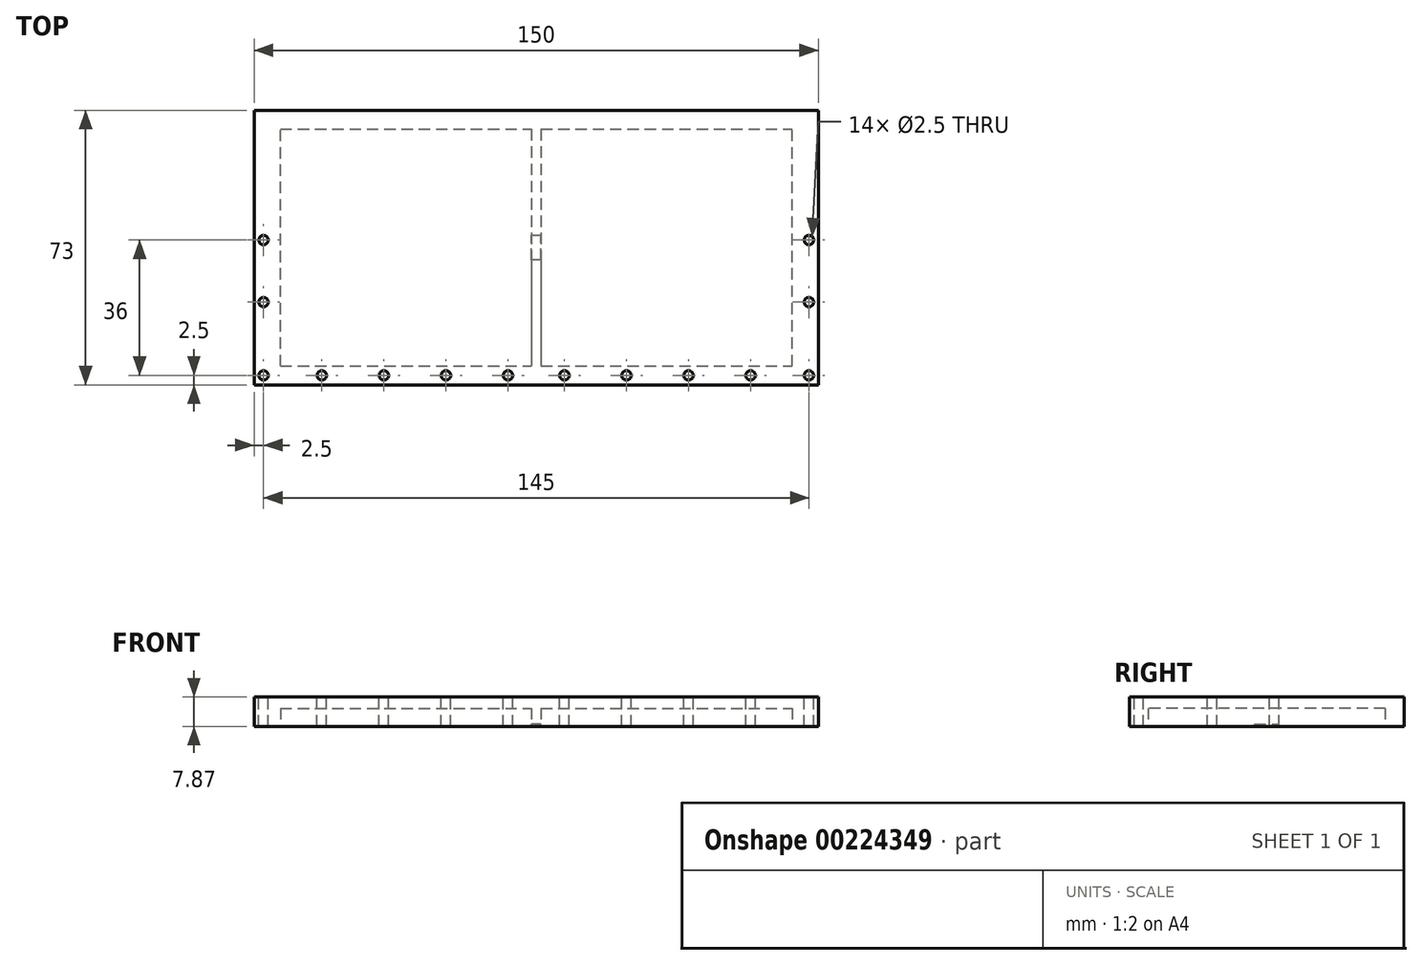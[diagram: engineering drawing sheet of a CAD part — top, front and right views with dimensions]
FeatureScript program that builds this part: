
annotation { "Feature Type Name" : "Feature", "Feature Type Description" : "" }
export const myFeature = defineFeature(function(context is Context, id is Id, definition is map)
    precondition{}
    {
        {
            var Q0;
            Q0=qCreatedBy(makeId("Top.planeOp"),FACE);
            var sketch = newSketch(context, id + "F0", { "sketchPlane" : qUnion([Q0])});
            skLineSegment(sketch, "E0.bottom", {"start": v(0, 0) * mm, "end": v(150, 0) * mm});
            skLineSegment(sketch, "E0.top", {"start": v(0, 73) * mm, "end": v(150, 73) * mm});
            skLineSegment(sketch, "E0.left", {"start": v(0, 0) * mm, "end": v(0, 73) * mm});
            skLineSegment(sketch, "E0.right", {"start": v(150, 0) * mm, "end": v(150, 73) * mm});
            skSolve(sketch);
        }
        {
            var Q0;
            Q0 = qSketchRegion(id + "F0", true);
            extrude(context, id + "F1", {"entities" : qUnion([Q0]), "depth" : 7.87 * mm});
        }
        {
            var Q0;
            Q0=qCreatedBy(makeId("Top.planeOp"),FACE);
            var sketch = newSketch(context, id + "F2", { "sketchPlane" : qUnion([Q0])});
            skLineSegment(sketch, "E1.bottom", {"start": v(7, 5) * mm, "end": v(143, 5) * mm});
            skLineSegment(sketch, "E1.top", {"start": v(7, 68) * mm, "end": v(143, 68) * mm});
            skLineSegment(sketch, "E1.left", {"start": v(7, 5) * mm, "end": v(7, 68) * mm});
            skLineSegment(sketch, "E1.right", {"start": v(143, 5) * mm, "end": v(143, 68) * mm});
            skSolve(sketch);
        }
        {
            var Q0;
            Q0 = qSketchRegion(id + "F2", true);
            extrude(context, id + "F3", {"entities" : qUnion([Q0]), "operationType" : NewBodyOperationType.REMOVE, "depth" : 4.87 * mm});
        }
        {
            var Q0;
            Q0=qCreatedBy(makeId("Front.planeOp"),FACE);
            var sketch = newSketch(context, id + "F4", { "sketchPlane" : qUnion([Q0])});
            skLineSegment(sketch, "E2.bottom", {"start": v(73.75, 0) * mm, "end": v(76.25, 0) * mm});
            skLineSegment(sketch, "E2.top", {"start": v(73.75, 4.87) * mm, "end": v(76.25, 4.87) * mm});
            skLineSegment(sketch, "E2.left", {"start": v(73.75, 0) * mm, "end": v(73.75, 4.87) * mm});
            skLineSegment(sketch, "E2.right", {"start": v(76.25, 0) * mm, "end": v(76.25, 4.87) * mm});
            skSolve(sketch);
        }
        {
            var Q0;
            Q0 = qSketchRegion(id + "F4", true);
            extrude(context, id + "F5", {"entities" : qUnion([Q0]), "operationType" : NewBodyOperationType.ADD, "oppositeDirection" : true, "depth" : 73 * mm});
        }
        {
            var Q0;
            Q0=makeQuery(id+"F5.opExtrude","SWEPT_FACE",FACE,{"disambiguationData":[OSD([sQuery(id+"F4.wireOp",EDGE,"E2.left")])]});
            var sketch = newSketch(context, id + "F6", { "sketchPlane" : qUnion([Q0])});
            skLineSegment(sketch, "E3.bottom", {"start": v(-33.25, 0) * mm, "end": v(-39.75, 0) * mm});
            skLineSegment(sketch, "E3.top", {"start": v(-33.25, 0.62) * mm, "end": v(-39.75, 0.62) * mm});
            skLineSegment(sketch, "E3.left", {"start": v(-33.25, 0) * mm, "end": v(-33.25, 0.62) * mm});
            skLineSegment(sketch, "E3.right", {"start": v(-39.75, 0) * mm, "end": v(-39.75, 0.62) * mm});
            skSolve(sketch);
        }
        {
            var Q0;
            Q0=makeQuery(id+"F6.imprint","IMPRINT",FACE,{"disambiguationData":[TD([[makeQuery(id+"F6.imprint","IMPRINT",EDGE,{"derivedFrom":sQuery(id+"F6.wireOp",EDGE,"E3.bottom")}),1.0]])]});
            extrude(context, id + "F7", {"entities" : qUnion([Q0]), "operationType" : NewBodyOperationType.REMOVE, "oppositeDirection" : true, "depth" : 2.5 * mm});
        }
        {
            var Q0;
            Q0=makeQuery(id+"F1.opExtrude","CAP_FACE",FACE,{"disambiguationData":[OSD([sQuery(id+"F0.wireOp",EDGE,"E0.bottom"),sQuery(id+"F0.wireOp",EDGE,"E0.top"),sQuery(id+"F0.wireOp",EDGE,"E0.left"),sQuery(id+"F0.wireOp",EDGE,"E0.right")])],"isStart":false});
            var sketch = newSketch(context, id + "F8", { "sketchPlane" : qUnion([Q0])});
            skCircle(sketch, "E4", {"center": v(2.5, 2.5) * mm, "radius": 1.25 * mm});
            skSolve(sketch);
        }
        {
            var Q0;
            Q0 = qSketchRegion(id + "F8", true);
            extrude(context, id + "F9", {"entities" : qUnion([Q0]), "operationType" : NewBodyOperationType.REMOVE, "oppositeDirection" : true, "depth" : 7.87 * mm});
        }
        {
            var Q0;
            Q0=makeQuery(id+"F1.opExtrude","CAP_FACE",FACE,{"disambiguationData":[OSD([sQuery(id+"F0.wireOp",EDGE,"E0.bottom"),sQuery(id+"F0.wireOp",EDGE,"E0.top"),sQuery(id+"F0.wireOp",EDGE,"E0.left"),sQuery(id+"F0.wireOp",EDGE,"E0.right")])],"isStart":false});
            var sketch = newSketch(context, id + "F10", { "sketchPlane" : qUnion([Q0])});
            skCircle(sketch, "E5", {"center": v(18, 2.5) * mm, "radius": 1.25 * mm});
            skSolve(sketch);
        }
        {
            var Q0;
            Q0 = qSketchRegion(id + "F10", true);
            extrude(context, id + "F11", {"entities" : qUnion([Q0]), "operationType" : NewBodyOperationType.REMOVE, "oppositeDirection" : true, "depth" : 7.87 * mm});
        }
        {
            var Q0;
            Q0=makeQuery(id+"F1.opExtrude","CAP_FACE",FACE,{"disambiguationData":[OSD([sQuery(id+"F0.wireOp",EDGE,"E0.bottom"),sQuery(id+"F0.wireOp",EDGE,"E0.top"),sQuery(id+"F0.wireOp",EDGE,"E0.left"),sQuery(id+"F0.wireOp",EDGE,"E0.right")])],"isStart":false});
            var sketch = newSketch(context, id + "F12", { "sketchPlane" : qUnion([Q0])});
            skCircle(sketch, "E6", {"center": v(34.5, 2.5) * mm, "radius": 1.25 * mm});
            skSolve(sketch);
        }
        {
            var Q0;
            Q0 = qSketchRegion(id + "F12", true);
            extrude(context, id + "F13", {"entities" : qUnion([Q0]), "operationType" : NewBodyOperationType.REMOVE, "oppositeDirection" : true, "depth" : 7.87 * mm});
        }
        {
            var Q0;
            Q0=makeQuery(id+"F1.opExtrude","CAP_FACE",FACE,{"disambiguationData":[OSD([sQuery(id+"F0.wireOp",EDGE,"E0.bottom"),sQuery(id+"F0.wireOp",EDGE,"E0.top"),sQuery(id+"F0.wireOp",EDGE,"E0.left"),sQuery(id+"F0.wireOp",EDGE,"E0.right")])],"isStart":false});
            var sketch = newSketch(context, id + "F14", { "sketchPlane" : qUnion([Q0])});
            skCircle(sketch, "E7", {"center": v(51, 2.5) * mm, "radius": 1.25 * mm});
            skSolve(sketch);
        }
        {
            var Q0;
            Q0 = qSketchRegion(id + "F14", true);
            extrude(context, id + "F15", {"entities" : qUnion([Q0]), "operationType" : NewBodyOperationType.REMOVE, "oppositeDirection" : true, "depth" : 7.87 * mm});
        }
        {
            var Q0;
            Q0=makeQuery(id+"F1.opExtrude","CAP_FACE",FACE,{"disambiguationData":[OSD([sQuery(id+"F0.wireOp",EDGE,"E0.bottom"),sQuery(id+"F0.wireOp",EDGE,"E0.top"),sQuery(id+"F0.wireOp",EDGE,"E0.left"),sQuery(id+"F0.wireOp",EDGE,"E0.right")])],"isStart":false});
            var sketch = newSketch(context, id + "F16", { "sketchPlane" : qUnion([Q0])});
            skCircle(sketch, "E8", {"center": v(67.5, 2.5) * mm, "radius": 1.25 * mm});
            skSolve(sketch);
        }
        {
            var Q0;
            Q0 = qSketchRegion(id + "F16", true);
            extrude(context, id + "F17", {"entities" : qUnion([Q0]), "operationType" : NewBodyOperationType.REMOVE, "oppositeDirection" : true, "depth" : 7.87 * mm});
        }
        {
            var Q0;
            Q0=makeQuery(id+"F1.opExtrude","CAP_FACE",FACE,{"disambiguationData":[OSD([sQuery(id+"F0.wireOp",EDGE,"E0.bottom"),sQuery(id+"F0.wireOp",EDGE,"E0.top"),sQuery(id+"F0.wireOp",EDGE,"E0.left"),sQuery(id+"F0.wireOp",EDGE,"E0.right")])],"isStart":false});
            var sketch = newSketch(context, id + "F18", { "sketchPlane" : qUnion([Q0])});
            skCircle(sketch, "E9", {"center": v(82.5, 2.5) * mm, "radius": 1.25 * mm});
            skSolve(sketch);
        }
        {
            var Q0;
            Q0 = qSketchRegion(id + "F18", true);
            extrude(context, id + "F19", {"entities" : qUnion([Q0]), "operationType" : NewBodyOperationType.REMOVE, "oppositeDirection" : true, "depth" : 7.87 * mm});
        }
        {
            var Q0;
            Q0=makeQuery(id+"F1.opExtrude","CAP_FACE",FACE,{"disambiguationData":[OSD([sQuery(id+"F0.wireOp",EDGE,"E0.bottom"),sQuery(id+"F0.wireOp",EDGE,"E0.top"),sQuery(id+"F0.wireOp",EDGE,"E0.left"),sQuery(id+"F0.wireOp",EDGE,"E0.right")])],"isStart":false});
            var sketch = newSketch(context, id + "F20", { "sketchPlane" : qUnion([Q0])});
            skCircle(sketch, "E10", {"center": v(99, 2.5) * mm, "radius": 1.25 * mm});
            skSolve(sketch);
        }
        {
            var Q0;
            Q0 = qSketchRegion(id + "F20", true);
            extrude(context, id + "F21", {"entities" : qUnion([Q0]), "operationType" : NewBodyOperationType.REMOVE, "oppositeDirection" : true, "depth" : 7.87 * mm});
        }
        {
            var Q0;
            Q0=makeQuery(id+"F1.opExtrude","CAP_FACE",FACE,{"disambiguationData":[OSD([sQuery(id+"F0.wireOp",EDGE,"E0.bottom"),sQuery(id+"F0.wireOp",EDGE,"E0.top"),sQuery(id+"F0.wireOp",EDGE,"E0.left"),sQuery(id+"F0.wireOp",EDGE,"E0.right")])],"isStart":false});
            var sketch = newSketch(context, id + "F22", { "sketchPlane" : qUnion([Q0])});
            skCircle(sketch, "E11", {"center": v(115.5, 2.5) * mm, "radius": 1.25 * mm});
            skSolve(sketch);
        }
        {
            var Q0;
            Q0 = qSketchRegion(id + "F22", true);
            extrude(context, id + "F23", {"entities" : qUnion([Q0]), "operationType" : NewBodyOperationType.REMOVE, "oppositeDirection" : true, "depth" : 7.87 * mm});
        }
        {
            var Q0;
            Q0=makeQuery(id+"F1.opExtrude","CAP_FACE",FACE,{"disambiguationData":[OSD([sQuery(id+"F0.wireOp",EDGE,"E0.bottom"),sQuery(id+"F0.wireOp",EDGE,"E0.top"),sQuery(id+"F0.wireOp",EDGE,"E0.left"),sQuery(id+"F0.wireOp",EDGE,"E0.right")])],"isStart":false});
            var sketch = newSketch(context, id + "F24", { "sketchPlane" : qUnion([Q0])});
            skCircle(sketch, "E12", {"center": v(132, 2.5) * mm, "radius": 1.25 * mm});
            skSolve(sketch);
        }
        {
            var Q0;
            Q0 = qSketchRegion(id + "F24", true);
            extrude(context, id + "F25", {"entities" : qUnion([Q0]), "operationType" : NewBodyOperationType.REMOVE, "oppositeDirection" : true, "depth" : 7.87 * mm});
        }
        {
            var Q0;
            Q0=makeQuery(id+"F1.opExtrude","CAP_FACE",FACE,{"disambiguationData":[OSD([sQuery(id+"F0.wireOp",EDGE,"E0.bottom"),sQuery(id+"F0.wireOp",EDGE,"E0.top"),sQuery(id+"F0.wireOp",EDGE,"E0.left"),sQuery(id+"F0.wireOp",EDGE,"E0.right")])],"isStart":false});
            var sketch = newSketch(context, id + "F26", { "sketchPlane" : qUnion([Q0])});
            skCircle(sketch, "E13", {"center": v(147.5, 2.5) * mm, "radius": 1.25 * mm});
            skSolve(sketch);
        }
        {
            var Q0;
            Q0 = qSketchRegion(id + "F26", true);
            extrude(context, id + "F27", {"entities" : qUnion([Q0]), "operationType" : NewBodyOperationType.REMOVE, "oppositeDirection" : true, "depth" : 7.87 * mm});
        }
        {
            var Q0;
            Q0=makeQuery(id+"F1.opExtrude","CAP_FACE",FACE,{"disambiguationData":[OSD([sQuery(id+"F0.wireOp",EDGE,"E0.bottom"),sQuery(id+"F0.wireOp",EDGE,"E0.top"),sQuery(id+"F0.wireOp",EDGE,"E0.left"),sQuery(id+"F0.wireOp",EDGE,"E0.right")])],"isStart":false});
            var sketch = newSketch(context, id + "F28", { "sketchPlane" : qUnion([Q0])});
            skCircle(sketch, "E14", {"center": v(2.5, 22) * mm, "radius": 1.25 * mm});
            skSolve(sketch);
        }
        {
            var Q0;
            Q0 = qSketchRegion(id + "F28", true);
            extrude(context, id + "F29", {"entities" : qUnion([Q0]), "operationType" : NewBodyOperationType.REMOVE, "oppositeDirection" : true, "depth" : 7.87 * mm});
        }
        {
            var Q0;
            Q0=makeQuery(id+"F1.opExtrude","CAP_FACE",FACE,{"disambiguationData":[OSD([sQuery(id+"F0.wireOp",EDGE,"E0.bottom"),sQuery(id+"F0.wireOp",EDGE,"E0.top"),sQuery(id+"F0.wireOp",EDGE,"E0.left"),sQuery(id+"F0.wireOp",EDGE,"E0.right")])],"isStart":false});
            var sketch = newSketch(context, id + "F30", { "sketchPlane" : qUnion([Q0])});
            skCircle(sketch, "E15", {"center": v(147.5, 22) * mm, "radius": 1.25 * mm});
            skSolve(sketch);
        }
        {
            var Q0;
            Q0 = qSketchRegion(id + "F30", true);
            extrude(context, id + "F31", {"entities" : qUnion([Q0]), "operationType" : NewBodyOperationType.REMOVE, "oppositeDirection" : true, "depth" : 7.87 * mm});
        }
        {
            var Q0;
            Q0=makeQuery(id+"F1.opExtrude","CAP_FACE",FACE,{"disambiguationData":[OSD([sQuery(id+"F0.wireOp",EDGE,"E0.bottom"),sQuery(id+"F0.wireOp",EDGE,"E0.top"),sQuery(id+"F0.wireOp",EDGE,"E0.left"),sQuery(id+"F0.wireOp",EDGE,"E0.right")])],"isStart":false});
            var sketch = newSketch(context, id + "F32", { "sketchPlane" : qUnion([Q0])});
            skCircle(sketch, "E16", {"center": v(147.5, 38.5) * mm, "radius": 1.25 * mm});
            skSolve(sketch);
        }
        {
            var Q0;
            Q0 = qSketchRegion(id + "F32", true);
            extrude(context, id + "F33", {"entities" : qUnion([Q0]), "operationType" : NewBodyOperationType.REMOVE, "oppositeDirection" : true, "depth" : 7.87 * mm});
        }
        {
            var Q0;
            Q0=makeQuery(id+"F1.opExtrude","CAP_FACE",FACE,{"disambiguationData":[OSD([sQuery(id+"F0.wireOp",EDGE,"E0.bottom"),sQuery(id+"F0.wireOp",EDGE,"E0.top"),sQuery(id+"F0.wireOp",EDGE,"E0.left"),sQuery(id+"F0.wireOp",EDGE,"E0.right")])],"isStart":false});
            var sketch = newSketch(context, id + "F34", { "sketchPlane" : qUnion([Q0])});
            skCircle(sketch, "E17", {"center": v(2.5, 38.5) * mm, "radius": 1.25 * mm});
            skSolve(sketch);
        }
        {
            var Q0;
            Q0 = qSketchRegion(id + "F34", true);
            extrude(context, id + "F35", {"entities" : qUnion([Q0]), "operationType" : NewBodyOperationType.REMOVE, "oppositeDirection" : true, "depth" : 7.87 * mm});
        }
    });
